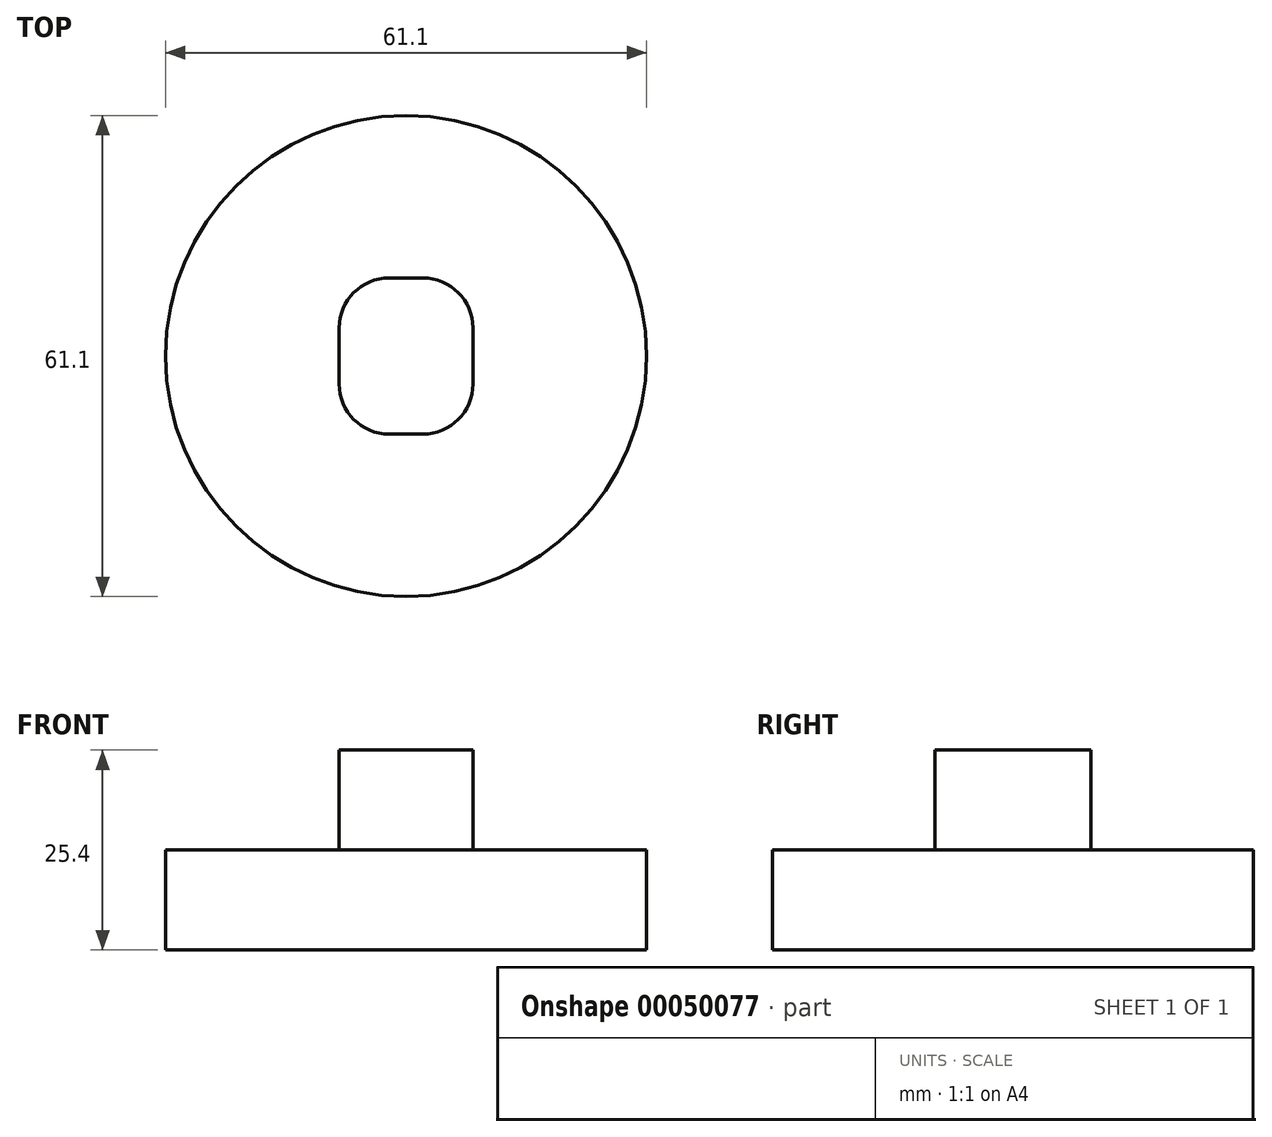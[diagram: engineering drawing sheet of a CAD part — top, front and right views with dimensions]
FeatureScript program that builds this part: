
annotation { "Feature Type Name" : "Feature", "Feature Type Description" : "" }
export const myFeature = defineFeature(function(context is Context, id is Id, definition is map)
    precondition{}
    {
        {
            var Q0;
            Q0=qCreatedBy(makeId("Top.planeOp"),FACE);
            var sketch = newSketch(context, id + "F0", { "sketchPlane" : qUnion([Q0])});
            skCircle(sketch, "E0", {"center": v(0, 0) * mm, "radius": 30.55 * mm});
            skSolve(sketch);
        }
        {
            var Q0;
            Q0=makeQuery(id+"F0.imprint","IMPRINT",FACE,{"disambiguationData":[TD([[makeQuery(id+"F0.imprint","IMPRINT",EDGE,{"derivedFrom":sQuery(id+"F0.wireOp",EDGE,"E0")}),1.0]])]});
            extrude(context, id + "F1", {"entities" : qUnion([Q0]), "depth" : 12.7 * mm});
        }
        {
            var Q0;
            Q0=makeQuery(id+"F1.opExtrude","CAP_FACE",FACE,{"disambiguationData":[OSD([sQuery(id+"F0.wireOp",EDGE,"E0")])],"isStart":false});
            var sketch = newSketch(context, id + "F2", { "sketchPlane" : qUnion([Q0])});
            skLineSegment(sketch, "E1.rect.bottom", {"start": v(2.14, 9.92) * mm, "end": v(-2.14, 9.92) * mm});
            skLineSegment(sketch, "E1.rect.top", {"start": v(2.14, -9.92) * mm, "end": v(-2.14, -9.92) * mm});
            skLineSegment(sketch, "E1.rect.left", {"start": v(8.5, 3.57) * mm, "end": v(8.5, -3.57) * mm});
            skLineSegment(sketch, "E1.rect.right", {"start": v(-8.5, 3.57) * mm, "end": v(-8.5, -3.57) * mm});
            skPoint(sketch, "E1.rect.middle", {"position": v(0, 0) * mm});
            skPoint(sketch, "E2.visualSharp", {"position": v(-8.5, 9.92) * mm});
            skArc(sketch, "E2.filletArc", {"start": v(-2.14, 9.92) * mm, "mid": v(-6.63, 8.06) * mm, "end": v(-8.5, 3.57) * mm});
            skPoint(sketch, "E3.visualSharp", {"position": v(8.5, 9.92) * mm});
            skArc(sketch, "E3.filletArc", {"start": v(8.5, 3.57) * mm, "mid": v(6.63, 8.06) * mm, "end": v(2.14, 9.92) * mm});
            skPoint(sketch, "E4.visualSharp", {"position": v(-8.5, -9.92) * mm});
            skArc(sketch, "E4.filletArc", {"start": v(-8.5, -3.57) * mm, "mid": v(-6.63, -8.06) * mm, "end": v(-2.14, -9.92) * mm});
            skPoint(sketch, "E5.visualSharp", {"position": v(8.5, -9.92) * mm});
            skArc(sketch, "E5.filletArc", {"start": v(2.14, -9.92) * mm, "mid": v(6.63, -8.06) * mm, "end": v(8.5, -3.57) * mm});
            skSolve(sketch);
        }
        {
            var Q0;
            Q0=makeQuery(id+"F2.imprint","IMPRINT",FACE,{"disambiguationData":[TD([[makeQuery(id+"F2.imprint","IMPRINT",EDGE,{"derivedFrom":sQuery(id+"F2.wireOp",EDGE,"E1.rect.bottom")}),1.0]])]});
            extrude(context, id + "F3", {"entities" : qUnion([Q0]), "operationType" : NewBodyOperationType.ADD, "depth" : 12.7 * mm});
        }
    });
